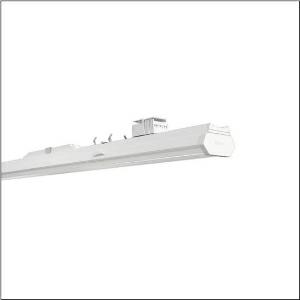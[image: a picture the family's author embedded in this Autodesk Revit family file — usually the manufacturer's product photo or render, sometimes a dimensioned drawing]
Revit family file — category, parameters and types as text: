
# Revit family: licross_11_protected_mo_51tp12dn495g3s
name_source: partatom
category: Lighting Fixtures
units: mm (PartAtom-declared; Revit-internal decimal feet)

## family parameters
Cut with Voids When Loaded = No
Host = Face
Light Source = No
Part Type = Normal
Room Calculation Point = No
Round Connector Dimension = Use Diameter
Shared = No

## types (1)
- --- (1 x LED, 980 lm, 6.8 W, 4000K)
    Apparent Load = 7 VA
    CIE Flux Codes = 73 92 98 99 100
    Color Rendering = 80
    Color Temperature = 4000K
    Default Elevation = 1800 mm
    Description = Licross 11 Protected MO, luminaire insert, of sheet steel, galvanised, coil coated, white, length: 1.500mm, width: 90mm, height: 101mm, LED rated luminous flux: 9.980lm, light colour: 840, SDCM (Standard Deviation of Colour Matching)MacAdam ≤ 2 SDCM (initial), control gear: DALI 2 (for two DALI lines), with plug, 6-pole, with phase selection, for trunking rail, 14-core, mains connection: 220..240V, AC, 50/60Hz, rated input power: 61W, for trunking rail, 14-core, internal wiring halogen-free, for emergency light function, converter,control gear: single battery element, battery: LiFePO4, 9Ah, primary light control with lens, of plastic, primary optical cover: cover, of PMMA, light emission: direct distribution, primary light characteristic: symmetric, protection rating (complete): IP64, insulation class (complete): insulation class I (protective earthing), certification: CE, UKCA, protection symbol: D if used in an environment with conductive dust loads with corresponding accessories, impact resistance: IK06, permissible ambient temperature for indoor applications: +5..+35°C, standard: EN 60598-2-22, LABS conformity tested according to VDMA 24364:2018-05, reducing of maximum allowable ambient temperature of 5°C with ceiling mounting, corresponds to IFS (International Featured Standards) requirements for safety and quality in the food industry, The light source and the operating device comply with the requirements of the Ecodesign Regulation (EU) 2019/2020 and are replaceable in accordance with this regulation, packaging unit: 1 piece
    Height = 92 mm
    Lamp = 1 x LED
    Lamp Light Flux = 980 lm
    Lamp Power = 6.8 W
    Lamp count = 1
    Length = 1500 mm
    Luminous efficacy = 144 lm/W
    Manufacturer = Siteco
    ModVariant = No
    Model = 51TP12DN495G3S
    Mounting Place = Ceiling
    Mounting Type = Pendant
    Number of Poles = 1
    OnlyDefault = Yes
    Power Factor = 1
    Product Name = Licross 11 Protected MO
    Product group = luminaire insert | ceiling pendant
    ProductGroupID = 901
    Protection Class = Protection class I
    Protection Degree = IP 64
    RLX_Detail_Level = 1
    RLX_Emergency_Light_Flux = 0 lm
    RLX_Emergency_Type = 0
    RLX_Emergency_Type_DB = No
    RlxData = <blob elided: 25153 chars, md5=ef5cd403>
    Socket = socket
    Standby Power = 0 W
    System Light Flux = 980 lm
    System Power = 7 W
    Type Comments = : emergency light operation: 3 h
    Type Image = l_1256148.jpg
    URL = http://relux.com
    VarID = @adj_094611
    Voltage = 0 V
    Weight = 0.00 kg
    Width = 88 mm

## geometry (parser evidence)
native form markers: Blend x4, Sweep x10
no freeform markers — native parametric forms only
